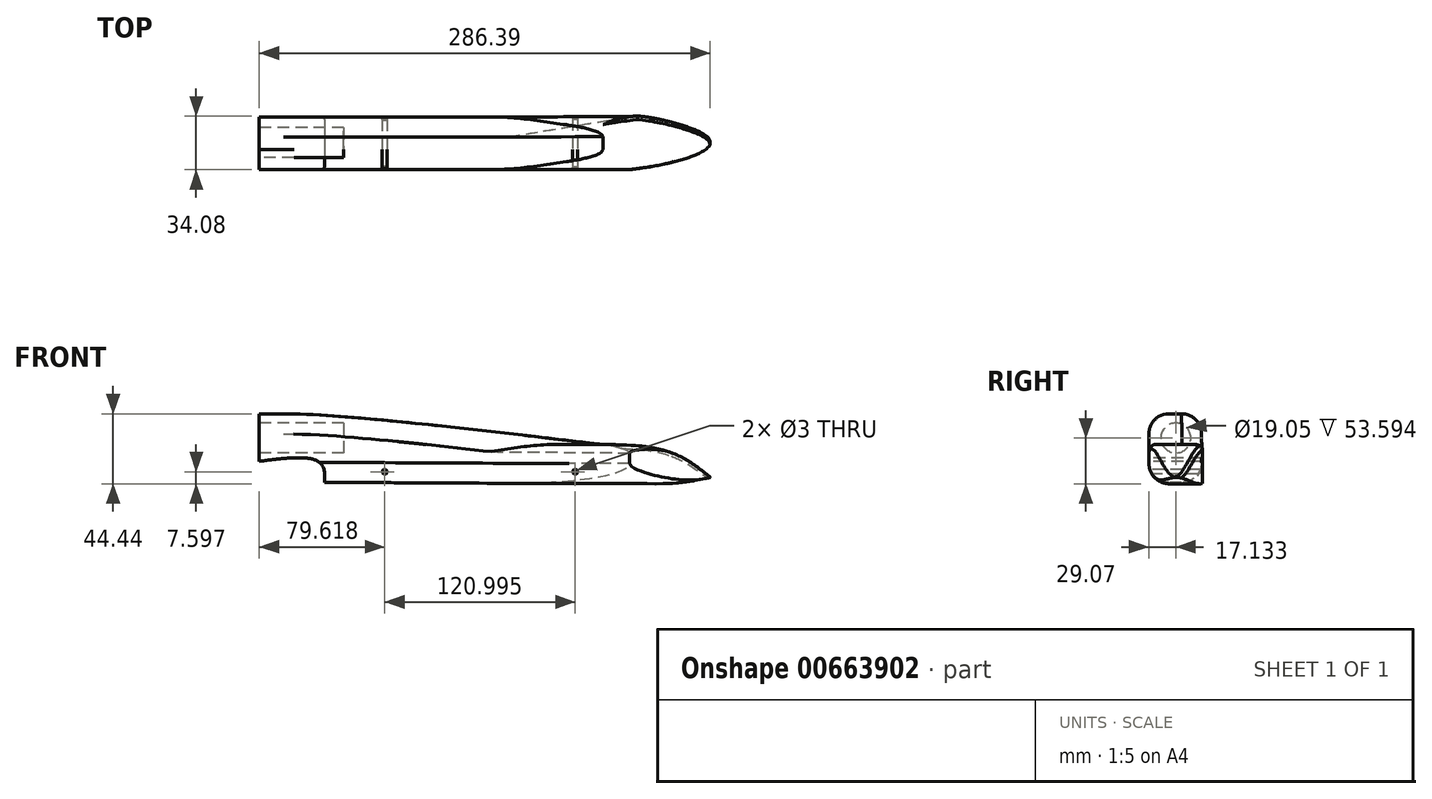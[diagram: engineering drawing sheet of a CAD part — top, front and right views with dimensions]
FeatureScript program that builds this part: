
annotation { "Feature Type Name" : "Feature", "Feature Type Description" : "" }
export const myFeature = defineFeature(function(context is Context, id is Id, definition is map)
    precondition{}
    {
        {
            var Q0;
            Q0=qCreatedBy(makeId("Front.planeOp"),FACE);
            var sketch = newSketch(context, id + "F0", { "sketchPlane" : qUnion([Q0])});
            skLineSegment(sketch, "E0", {"start": v(0, 0) * mm, "end": v(304.8, 0) * mm});
            skLineSegment(sketch, "E1", {"start": v(0, 0) * mm, "end": v(0, 69.85) * mm});
            skLineSegment(sketch, "E2", {"start": v(304.8, 0) * mm, "end": v(304.8, 15.88) * mm});
            skLineSegment(sketch, "E3", {"start": v(304.8, 15.88) * mm, "end": v(0, 69.85) * mm});
            skSolve(sketch);
        }
        {
            var Q0;
            Q0 = qSketchRegion(id + "F0", true);
            extrude(context, id + "F1", {"entities" : qUnion([Q0]), "depth" : 41.27 * mm, "offsetDistance" : 25.4 * mm});
        }
        {
            var Q0;
            Q0=makeQuery(id+"F1.opExtrude","SWEPT_FACE",FACE,{"disambiguationData":[OSD([sQuery(id+"F0.wireOp",EDGE,"E1")])]});
            var sketch = newSketch(context, id + "F2", { "sketchPlane" : qUnion([Q0])});
            skCircle(sketch, "E4", {"center": v(20.64, 31.75) * mm, "radius": 9.53 * mm});
            skSolve(sketch);
        }
        {
            var Q0;
            Q0=makeQuery(id+"F2.imprint","IMPRINT",FACE,{"disambiguationData":[TD([[makeQuery(id+"F2.imprint","IMPRINT",EDGE,{"derivedFrom":sQuery(id+"F2.wireOp",EDGE,"E4")}),1.0]])]});
            extrude(context, id + "F3", {"entities" : qUnion([Q0]), "operationType" : NewBodyOperationType.REMOVE, "oppositeDirection" : true, "depth" : 53.6 * mm, "offsetDistance" : 25.4 * mm});
        }
        {
            var Q0;
            Q0=makeQuery(id+"F1.opExtrude","CAP_FACE",FACE,{"disambiguationData":[OSD([sQuery(id+"F0.wireOp",EDGE,"E0"),sQuery(id+"F0.wireOp",EDGE,"E1"),sQuery(id+"F0.wireOp",EDGE,"E2"),sQuery(id+"F0.wireOp",EDGE,"E3")])],"isStart":false});
            var sketch = newSketch(context, id + "F4", { "sketchPlane" : qUnion([Q0])});
            skFitSpline(sketch, "E5", {"points": [v(0, 47.06) * mm, v(45.85, 45.85) * mm, v(282.5, 19.82) * mm], "startDerivative": vector(121.3, 1.13) * mm, "endDerivative": vector(406.6, -49.07) * mm});
            skFitSpline(sketch, "E6", {"points": [v(0, 16.92) * mm, v(38.47, 16.04) * mm, v(41.2, 0) * mm], "startDerivative": vector(80.62, 10.45) * mm, "endDerivative": vector(-4.2, -48.45) * mm});
            skFitSpline(sketch, "E7", {"points": [v(218.16, 27.56) * mm, v(261.99, 22.3) * mm, v(294.13, 0) * mm], "startDerivative": vector(89.94, -0.7) * mm, "endDerivative": vector(61.78, -54.54) * mm});
            skSolve(sketch);
        }
        {
            var Q0;
            {var subQ1=makeQuery(id+"F1.opExtrude","CAP_EDGE",EDGE,{"disambiguationData":[OSD([sQuery(id+"F0.wireOp",EDGE,"E1")])],"isStart":false});var subQ3=sQuery(id+"F4.wireOp",EDGE,"E5");var subQ4=makeQuery(id+"F4.imprint","INTERSECT",VERTEX,{"derivedFrom":[subQ1,subQ3]});Q0=makeQuery(id+"F4.imprint","IMPRINT",FACE,{"disambiguationData":[TD([[makeQuery(id+"F4.imprint","IMPRINT",EDGE,{"disambiguationData":[TD([[subQ4,-1.0]])],"derivedFrom":subQ3}),1.0]])]});}
            var Q1;
            {var subQ0=sQuery(id+"F4.wireOp",EDGE,"E6");Q1=makeQuery(id+"F4.imprint","IMPRINT",FACE,{"disambiguationData":[TD([[makeQuery(id+"F4.imprint","IMPRINT",EDGE,{"derivedFrom":subQ0}),-1.0]])]});}
            var Q2;
            {var subQ0=makeQuery(id+"F1.opExtrude","CAP_EDGE",EDGE,{"disambiguationData":[OSD([sQuery(id+"F0.wireOp",EDGE,"E2")])],"isStart":false});Q2=makeQuery(id+"F4.imprint","IMPRINT",FACE,{"disambiguationData":[TD([[makeQuery(id+"F4.imprint","IMPRINT",EDGE,{"derivedFrom":subQ0}),1.0]])]});}
            extrude(context, id + "F5", {"entities" : qUnion([Q0, Q1, Q2]), "operationType" : NewBodyOperationType.REMOVE, "oppositeDirection" : true, "depth" : 127 * mm, "offsetDistance" : 25.4 * mm});
        }
        {
            var Q0;
            Q0=makeQuery(id+"F1.opExtrude","CAP_FACE",FACE,{"disambiguationData":[OSD([sQuery(id+"F0.wireOp",EDGE,"E0"),sQuery(id+"F0.wireOp",EDGE,"E1"),sQuery(id+"F0.wireOp",EDGE,"E2"),sQuery(id+"F0.wireOp",EDGE,"E3")])],"isStart":false});
            var sketch = newSketch(context, id + "F6", { "sketchPlane" : qUnion([Q0])});
            skFitSpline(sketch, "E8", {"points": [v(41.48, 3.58) * mm, v(219.03, 2.73) * mm, v(245.4, 2.73) * mm, v(256.63, 2.73) * mm, v(271.78, 3.85) * mm, v(286.45, 6.69) * mm], "startDerivative": vector(478.64, -2.77) * mm, "endDerivative": vector(109.9, 24.41) * mm});
            skSolve(sketch);
        }
        {
            var Q0;
            {var subQ0=sQuery(id+"F6.wireOp",EDGE,"E8");Q0=makeQuery(id+"F6.imprint","IMPRINT",FACE,{"disambiguationData":[TD([[makeQuery(id+"F6.imprint","IMPRINT",EDGE,{"derivedFrom":subQ0}),-1.0]])]});}
            extrude(context, id + "F7", {"entities" : qUnion([Q0]), "operationType" : NewBodyOperationType.REMOVE, "oppositeDirection" : true, "depth" : 127 * mm, "offsetDistance" : 25.4 * mm});
        }
        {
            var Q0;
            Q0=qCreatedBy(makeId("Top.planeOp"),FACE);
            var sketch = newSketch(context, id + "F8", { "sketchPlane" : qUnion([Q0])});
            skFitSpline(sketch, "E9", {"points": [v(15.38, -4.3) * mm, v(235.01, -4.12) * mm], "startDerivative": vector(219.66, 0.09) * mm, "endDerivative": vector(219.66, 0.09) * mm});
            skFitSpline(sketch, "E10", {"points": [v(235.01, -4.12) * mm, v(245, -4.12) * mm, v(286.26, -19) * mm, v(235.01, -37.69) * mm], "startDerivative": vector(35.43, 5.86) * mm, "endDerivative": vector(-200.2, -21.78) * mm});
            skFitSpline(sketch, "E11", {"points": [v(235.01, -37.69) * mm, v(21.7, -37.69) * mm], "startDerivative": vector(-218.84, 0) * mm, "endDerivative": vector(-218.84, 0) * mm});
            skLineSegment(sketch, "E12", {"start": v(15.38, -4.3) * mm, "end": v(0, -4.3) * mm});
            skLineSegment(sketch, "E13", {"start": v(0, -37.77) * mm, "end": v(21.7, -37.69) * mm});
            skFitSpline(sketch, "E14.0", {"points": [v(41.48, -41.28) * mm, v(113.37, -41.28) * mm, v(212.98, -41.28) * mm, v(244.2, -41.28) * mm, v(256.57, -41.28) * mm, v(272.03, -41.28) * mm, v(281.66, -41.28) * mm, v(286.45, -41.28) * mm]});
            skLineSegment(sketch, "E15.0", {"start": v(286.45, 0) * mm, "end": v(286.45, -41.28) * mm});
            skFitSpline(sketch, "E16.0", {"points": [v(41.48, 0) * mm, v(113.37, 0) * mm, v(212.98, 0) * mm, v(244.2, 0) * mm, v(256.57, 0) * mm, v(272.03, 0) * mm, v(281.66, 0) * mm, v(286.45, 0) * mm]});
            skLineSegment(sketch, "E17.0", {"start": v(0, 0) * mm, "end": v(0, -4.3) * mm});
            skLineSegment(sketch, "E18.trimOffspring", {"start": v(0, -37.77) * mm, "end": v(0, -41.28) * mm});
            skLineSegment(sketch, "E19", {"start": v(0, -41.28) * mm, "end": v(41.48, -41.28) * mm});
            skLineSegment(sketch, "E20", {"start": v(0, 0) * mm, "end": v(41.48, 0) * mm});
            skSolve(sketch);
        }
        {
            var Q0;
            {var subQ1=sQuery(id+"F8.wireOp",EDGE,"E11");Q0=makeQuery(id+"F8.imprint","IMPRINT",FACE,{"disambiguationData":[TD([[makeQuery(id+"F8.imprint","IMPRINT",EDGE,{"derivedFrom":subQ1}),1.0]])]});}
            var Q1;
            {var subQ4=sQuery(id+"F8.wireOp",EDGE,"E9");Q1=makeQuery(id+"F8.imprint","IMPRINT",FACE,{"disambiguationData":[TD([[makeQuery(id+"F8.imprint","IMPRINT",EDGE,{"derivedFrom":subQ4}),1.0]])]});}
            extrude(context, id + "F9", {"entities" : qUnion([Q0, Q1]), "operationType" : NewBodyOperationType.REMOVE, "depth" : 60.96 * mm, "offsetDistance" : 25.4 * mm});
        }
        {
            var Q0;
            Q0=makeQuery(id+"F9.boolean.opBoolean","INTERSECT",EDGE,{"derivedFrom":[makeQuery(id+"F5.boolean.opBoolean","COPY",FACE,{"derivedFrom":makeQuery(id+"F5.opExtrude","SWEPT_FACE",FACE,{"disambiguationData":[OSD([sQuery(id+"F4.wireOp",EDGE,"E5")])]})}),makeQuery(id+"F9.opExtrude","SWEPT_FACE",FACE,{"disambiguationData":[OSD([sQuery(id+"F8.wireOp",EDGE,"E9")])]})]});
            var Q1;
            Q1=makeQuery(id+"F9.boolean.opBoolean","INTERSECT",EDGE,{"derivedFrom":[makeQuery(id+"F5.boolean.opBoolean","COPY",FACE,{"derivedFrom":makeQuery(id+"F5.opExtrude","SWEPT_FACE",FACE,{"disambiguationData":[OSD([sQuery(id+"F4.wireOp",EDGE,"E5")])]})}),makeQuery(id+"F9.opExtrude","SWEPT_FACE",FACE,{"disambiguationData":[OSD([sQuery(id+"F8.wireOp",EDGE,"E11")])]})]});
            fillet(context, id + "F10", {"entities" : qUnion([Q0, Q1]), "radius" : 12.7 * mm, "tangentPropagation" : true, "allowEdgeOverflow" : false});
        }
        {
            var Q0;
            Q0=makeQuery(id+"F9.boolean.opBoolean","INTERSECT",EDGE,{"derivedFrom":[makeQuery(id+"F5.boolean.opBoolean","COPY",FACE,{"derivedFrom":makeQuery(id+"F5.opExtrude","SWEPT_FACE",FACE,{"disambiguationData":[OSD([sQuery(id+"F4.wireOp",EDGE,"E7")])]})}),makeQuery(id+"F9.opExtrude","SWEPT_FACE",FACE,{"disambiguationData":[OSD([sQuery(id+"F8.wireOp",EDGE,"E11")])]})]});
            var Q1;
            {var subQ0=makeQuery(id+"F9.opExtrude","SWEPT_FACE",FACE,{"disambiguationData":[OSD([sQuery(id+"F8.wireOp",EDGE,"E11")])]});Q1=makeQuery(id+"F10.opFillet","BLEND_EDGE",EDGE,{"blendedFrom":[makeQuery(id+"F9.boolean.opBoolean","INTERSECT",EDGE,{"derivedFrom":[makeQuery(id+"F5.boolean.opBoolean","COPY",FACE,{"derivedFrom":makeQuery(id+"F5.opExtrude","SWEPT_FACE",FACE,{"disambiguationData":[OSD([sQuery(id+"F4.wireOp",EDGE,"E5")])]})}),subQ0]}),makeQuery(id+"F9.boolean.opBoolean","COPY",FACE,{"derivedFrom":subQ0})],"blendedInto":[makeQuery(id+"F9.boolean.opBoolean","COPY",FACE,{"derivedFrom":subQ0})]});}
            var Q2;
            Q2=makeQuery(id+"F9.boolean.opBoolean","INTERSECT",EDGE,{"derivedFrom":[makeQuery(id+"F5.boolean.opBoolean","COPY",FACE,{"derivedFrom":makeQuery(id+"F5.opExtrude","SWEPT_FACE",FACE,{"disambiguationData":[OSD([sQuery(id+"F4.wireOp",EDGE,"E7")])]})}),makeQuery(id+"F9.opExtrude","SWEPT_FACE",FACE,{"disambiguationData":[OSD([sQuery(id+"F8.wireOp",EDGE,"E9")])]})]});
            var Q3;
            {var subQ0=makeQuery(id+"F9.opExtrude","SWEPT_FACE",FACE,{"disambiguationData":[OSD([sQuery(id+"F8.wireOp",EDGE,"E9")])]});Q3=makeQuery(id+"F10.opFillet","BLEND_EDGE",EDGE,{"blendedFrom":[makeQuery(id+"F9.boolean.opBoolean","INTERSECT",EDGE,{"derivedFrom":[makeQuery(id+"F5.boolean.opBoolean","COPY",FACE,{"derivedFrom":makeQuery(id+"F5.opExtrude","SWEPT_FACE",FACE,{"disambiguationData":[OSD([sQuery(id+"F4.wireOp",EDGE,"E5")])]})}),subQ0]}),makeQuery(id+"F9.boolean.opBoolean","COPY",FACE,{"derivedFrom":subQ0})],"blendedInto":[makeQuery(id+"F9.boolean.opBoolean","COPY",FACE,{"derivedFrom":subQ0})]});}
            fillet(context, id + "F11", {"entities" : qUnion([Q0, Q1, Q2, Q3]), "radius" : 5.08 * mm, "tangentPropagation" : true, "allowEdgeOverflow" : false});
        }
        {
            var Q0;
            Q0=makeQuery(id+"F9.boolean.opBoolean","INTERSECT",EDGE,{"derivedFrom":[makeQuery(id+"F7.boolean.opBoolean","COPY",FACE,{"derivedFrom":makeQuery(id+"F7.opExtrude","SWEPT_FACE",FACE,{"disambiguationData":[OSD([sQuery(id+"F6.wireOp",EDGE,"E8")])]})}),makeQuery(id+"F9.opExtrude","SWEPT_FACE",FACE,{"disambiguationData":[OSD([sQuery(id+"F8.wireOp",EDGE,"E11")])]})]});
            var Q1;
            Q1=makeQuery(id+"F9.boolean.opBoolean","INTERSECT",EDGE,{"derivedFrom":[makeQuery(id+"F7.boolean.opBoolean","COPY",FACE,{"derivedFrom":makeQuery(id+"F7.opExtrude","SWEPT_FACE",FACE,{"disambiguationData":[OSD([sQuery(id+"F6.wireOp",EDGE,"E8")])]})}),makeQuery(id+"F9.opExtrude","SWEPT_FACE",FACE,{"disambiguationData":[OSD([sQuery(id+"F8.wireOp",EDGE,"E9")])]})]});
            fillet(context, id + "F12", {"entities" : qUnion([Q0, Q1]), "radius" : 12.7 * mm, "tangentPropagation" : true, "allowEdgeOverflow" : false});
        }
        {
            var Q0;
            {var subQ0=sQuery(id+"F8.wireOp",EDGE,"E10");Q0=makeQuery(id+"F9.boolean.opBoolean","INTERSECT",EDGE,{"derivedFrom":[makeQuery(id+"F5.boolean.opBoolean","COPY",FACE,{"derivedFrom":makeQuery(id+"F5.opExtrude","SWEPT_FACE",FACE,{"disambiguationData":[OSD([sQuery(id+"F4.wireOp",EDGE,"E7")])]})}),makeQuery(id+"F9.opExtrude","SWEPT_FACE",FACE,{"disambiguationData":[OSD([subQ0]),TDD([makeQuery(id+"F8.imprint","IMPRINT",EDGE,{"disambiguationData":[TD([[makeQuery(id+"F8.imprint","INTERSECT",VERTEX,{"derivedFrom":[sQuery(id+"F8.wireOp",EDGE,"E9"),subQ0]}),-1.0]])],"derivedFrom":subQ0})])]})]});}
            fillet(context, id + "F13", {"entities" : qUnion([Q0]), "radius" : 2.3 * mm, "tangentPropagation" : true, "allowEdgeOverflow" : false});
        }
        {
            var Q0;
            Q0=makeQuery(id+"F9.boolean.opBoolean","COPY",FACE,{"derivedFrom":makeQuery(id+"F9.opExtrude","SWEPT_FACE",FACE,{"disambiguationData":[OSD([sQuery(id+"F8.wireOp",EDGE,"E11")])]})});
            var sketch = newSketch(context, id + "F14", { "sketchPlane" : qUnion([Q0])});
            skCircle(sketch, "E21", {"center": v(79.62, 10.28) * mm, "radius": 1.5 * mm});
            skCircle(sketch, "E22", {"center": v(200.61, 10.28) * mm, "radius": 1.5 * mm});
            skSolve(sketch);
        }
        {
            var Q0;
            Q0 = qSketchRegion(id + "F14", true);
            extrude(context, id + "F15", {"entities" : qUnion([Q0]), "operationType" : NewBodyOperationType.REMOVE, "oppositeDirection" : true, "depth" : 76.2 * mm, "offsetDistance" : 25.4 * mm});
        }
    });
